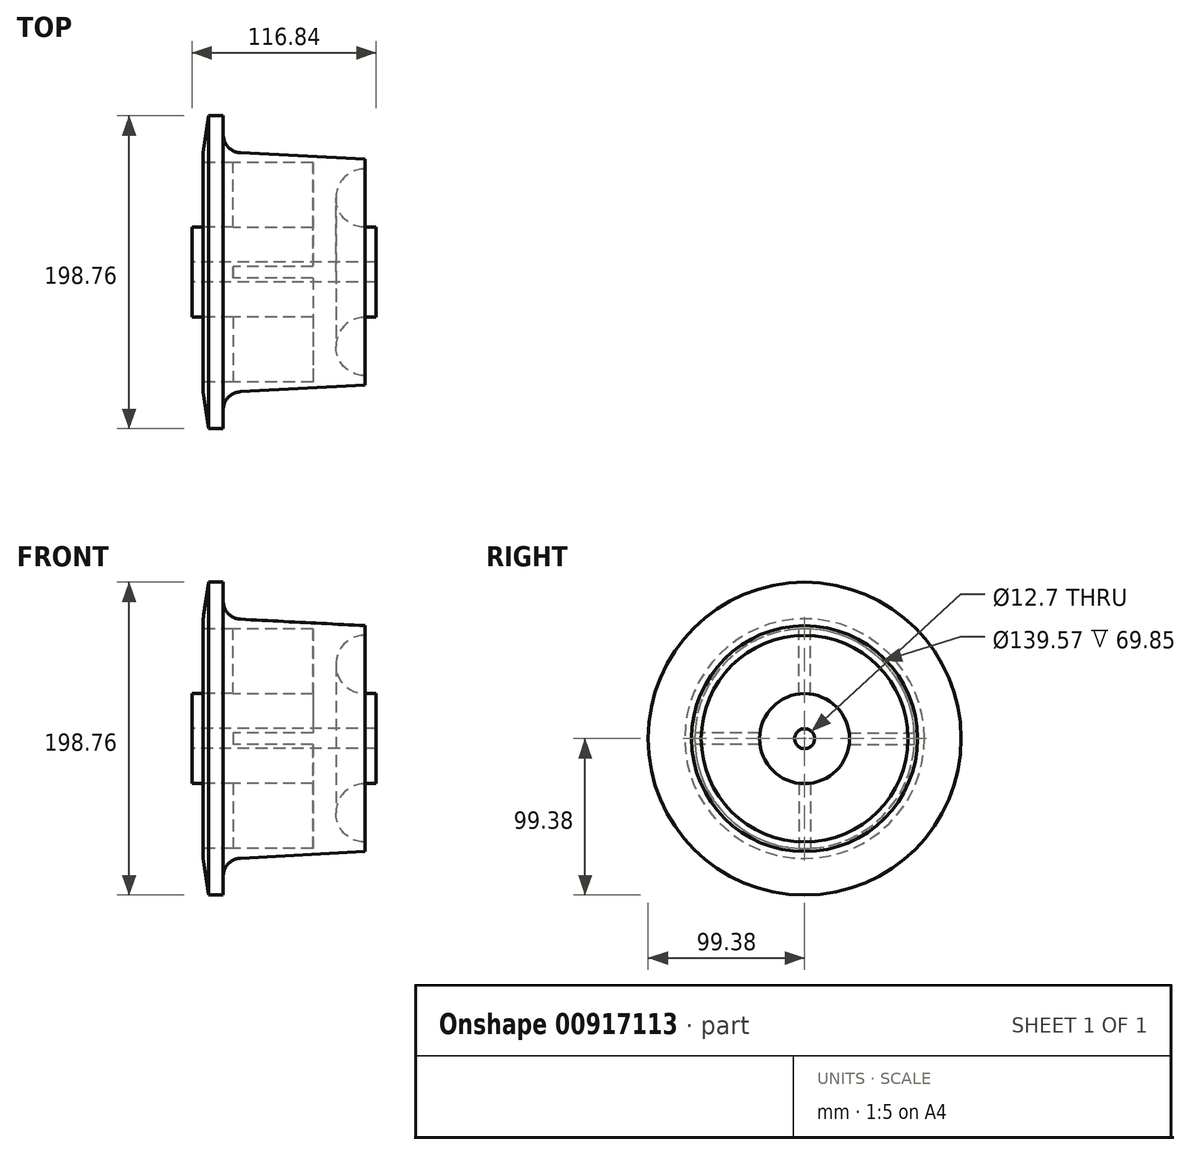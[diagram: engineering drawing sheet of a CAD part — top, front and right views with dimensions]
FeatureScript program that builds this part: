
annotation { "Feature Type Name" : "Feature", "Feature Type Description" : "" }
export const myFeature = defineFeature(function(context is Context, id is Id, definition is map)
    precondition{}
    {
        {
            var Q0;
            Q0=qCreatedBy(makeId("Front.planeOp"),FACE);
            var sketch = newSketch(context, id + "F0", { "sketchPlane" : qUnion([Q0])});
            skLineSegment(sketch, "E0", {"start": v(0, 6.35) * mm, "end": v(0, 0) * mm, "construction": true});
            skLineSegment(sketch, "E1", {"start": v(0, 6.35) * mm, "end": v(116.84, 6.35) * mm});
            skLineSegment(sketch, "E2", {"start": v(116.84, 6.35) * mm, "end": v(116.84, 28.58) * mm});
            skLineSegment(sketch, "E3", {"start": v(116.84, 28.58) * mm, "end": v(0, 28.58) * mm});
            skLineSegment(sketch, "E4", {"start": v(0, 28.58) * mm, "end": v(0, 6.35) * mm});
            skLineSegment(sketch, "E5", {"start": v(109.85, 28.58) * mm, "end": v(109.85, 71.76) * mm});
            skLineSegment(sketch, "E6", {"start": v(0, 99.38) * mm, "end": v(-18.57, 99.38) * mm, "construction": true});
            skLineSegment(sketch, "E7", {"start": v(6.99, 28.58) * mm, "end": v(6.99, 68.9) * mm});
            skLineSegment(sketch, "E8", {"start": v(6.99, 68.9) * mm, "end": v(21.01, 68.9) * mm, "construction": true});
            skLineSegment(sketch, "E9", {"start": v(6.99, 68.9) * mm, "end": v(6.99, 76.14) * mm});
            skLineSegment(sketch, "E10", {"start": v(6.99, 99.38) * mm, "end": v(10.54, 99.38) * mm, "construction": true});
            skLineSegment(sketch, "E11", {"start": v(6.99, 76.14) * mm, "end": v(10.54, 99.38) * mm});
            skLineSegment(sketch, "E12", {"start": v(10.54, 99.38) * mm, "end": v(19.81, 99.38) * mm});
            skLineSegment(sketch, "E13", {"start": v(19.81, 99.38) * mm, "end": v(19.81, 87.31) * mm});
            skLineSegment(sketch, "E14", {"start": v(109.85, 71.76) * mm, "end": v(30.64, 75.9) * mm});
            skArc(sketch, "E15", {"start": v(19.81, 87.31) * mm, "mid": v(22.95, 79.45) * mm, "end": v(30.64, 75.9) * mm});
            skLineSegment(sketch, "E16", {"start": v(0, 0) * mm, "end": v(91.98, 0) * mm, "construction": true});
            skPoint(sketch, "E17", {"position": v(22.95, 79.45) * mm});
            skSolve(sketch);
        }
        {
            var Q0;
            Q0=makeQuery(id+"F0.imprint","IMPRINT",FACE,{"disambiguationData":[TD([[makeQuery(id+"F0.imprint","IMPRINT",EDGE,{"derivedFrom":sQuery(id+"F0.wireOp",EDGE,"E1")}),1.0]])]});
            var Q1;
            {var subQ1=sQuery(id+"F0.wireOp",EDGE,"E5");Q1=makeQuery(id+"F0.imprint","IMPRINT",FACE,{"disambiguationData":[TD([[makeQuery(id+"F0.imprint","IMPRINT",EDGE,{"derivedFrom":subQ1}),1.0]])]});}
            var Q2;
            Q2=sQuery(id+"F0.wireOp",EDGE,"E16");
            revolve(context, id + "F1", {"surfaceOperationType" : NewSurfaceOperationType.NEW, "entities" : qUnion([Q0, Q1]), "axis" : qUnion([Q2]), "revolveType" : RevolveType.FULL});
        }
        {
            var Q0;
            Q0=qCreatedBy(makeId("Front.planeOp"),FACE);
            var sketch = newSketch(context, id + "F2", { "sketchPlane" : qUnion([Q0])});
            skLineSegment(sketch, "E18.0", {"start": v(109.85, -71.76) * mm, "end": v(109.85, 71.76) * mm});
            skLineSegment(sketch, "E19", {"start": v(109.85, 0) * mm, "end": v(85.08, 0) * mm, "construction": true});
            skLineSegment(sketch, "E20", {"start": v(109.85, 65.66) * mm, "end": v(128.1, 65.66) * mm, "construction": true});
            skLineSegment(sketch, "E21", {"start": v(109.85, 47.12) * mm, "end": v(125.43, 47.12) * mm, "construction": true});
            skArc(sketch, "E22", {"start": v(109.85, 65.66) * mm, "mid": v(91.31, 47.12) * mm, "end": v(109.85, 28.58) * mm});
            skSolve(sketch);
        }
        {
            var Q0;
            {var subQ0=sQuery(id+"F2.wireOp",EDGE,"E22");Q0=makeQuery(id+"F2.imprint","IMPRINT",FACE,{"disambiguationData":[TD([[makeQuery(id+"F2.imprint","IMPRINT",EDGE,{"derivedFrom":subQ0}),1.0]])]});}
            var Q1;
            Q1=sQuery(id+"F2.wireOp",EDGE,"E19");
            revolve(context, id + "F3", {"operationType" : NewBodyOperationType.REMOVE, "surfaceOperationType" : NewSurfaceOperationType.NEW, "entities" : qUnion([Q0]), "axis" : qUnion([Q1]), "revolveType" : RevolveType.FULL, "oppositeDirection" : true});
        }
        {
            var Q0;
            Q0=makeQuery(id+"F1.opRevolve","SWEPT_FACE",FACE,{"disambiguationData":[OSD([sQuery(id+"F0.wireOp",EDGE,"E7"),sQuery(id+"F0.wireOp",EDGE,"E9")])]});
            var sketch = newSketch(context, id + "F4", { "sketchPlane" : qUnion([Q0])});
            skCircle(sketch, "E23.0", {"center": v(0, 0) * mm, "radius": 76.14 * mm});
            skCircle(sketch, "E24.0", {"center": v(0, 0) * mm, "radius": 28.58 * mm});
            skLineSegment(sketch, "E25", {"start": v(0, 28.58) * mm, "end": v(0, 76.14) * mm, "construction": true});
            skLineSegment(sketch, "E26", {"start": v(28.58, 0) * mm, "end": v(76.14, 0) * mm, "construction": true});
            skLineSegment(sketch, "E27.0", {"start": v(3.62, 28.34) * mm, "end": v(3.62, 76.05) * mm});
            skLineSegment(sketch, "E28.0", {"start": v(-3.62, 28.34) * mm, "end": v(-3.62, 76.05) * mm});
            skLineSegment(sketch, "E29", {"start": v(0, 0) * mm, "end": v(14.85, 0) * mm, "construction": true});
            skLineSegment(sketch, "E30", {"start": v(0, 0) * mm, "end": v(0, 14.37) * mm, "construction": true});
            skLineSegment(sketch, "E31.0", {"start": v(28.34, -3.62) * mm, "end": v(76.05, -3.62) * mm});
            skLineSegment(sketch, "E32.0", {"start": v(28.34, 3.62) * mm, "end": v(76.05, 3.62) * mm});
            skLineSegment(sketch, "E33.MirrorCS", {"start": v(3.62, -28.34) * mm, "end": v(3.62, -76.05) * mm});
            skLineSegment(sketch, "E34.MirrorCS", {"start": v(-3.62, -28.34) * mm, "end": v(-3.62, -76.05) * mm});
            skLineSegment(sketch, "E35.MirrorCS", {"start": v(-28.34, 3.62) * mm, "end": v(-76.05, 3.62) * mm});
            skLineSegment(sketch, "E36.MirrorCS", {"start": v(-28.34, -3.62) * mm, "end": v(-76.05, -3.62) * mm});
            skCircle(sketch, "E37.0", {"center": v(0, 0) * mm, "radius": 69.79 * mm});
            skSolve(sketch);
        }
        {
            var Q0;
            {var subQ0=sQuery(id+"F4.wireOp",EDGE,"E31.0");var subQ1=sQuery(id+"F4.wireOp",EDGE,"E24.0");var subQ2=makeQuery(id+"F4.imprint","INTERSECT",VERTEX,{"derivedFrom":[subQ1,subQ0]});Q0=makeQuery(id+"F4.imprint","IMPRINT",FACE,{"disambiguationData":[TD([[makeQuery(id+"F4.imprint","IMPRINT",EDGE,{"disambiguationData":[TD([[subQ2,1.0]])],"derivedFrom":subQ1}),-1.0]])]});}
            var Q1;
            {var subQ0=sQuery(id+"F4.wireOp",EDGE,"E34.MirrorCS");var subQ1=sQuery(id+"F4.wireOp",EDGE,"E24.0");var subQ2=makeQuery(id+"F4.imprint","INTERSECT",VERTEX,{"derivedFrom":[subQ1,subQ0]});Q1=makeQuery(id+"F4.imprint","IMPRINT",FACE,{"disambiguationData":[TD([[makeQuery(id+"F4.imprint","IMPRINT",EDGE,{"disambiguationData":[TD([[subQ2,1.0]])],"derivedFrom":subQ1}),-1.0]])]});}
            var Q2;
            {var subQ0=sQuery(id+"F4.wireOp",EDGE,"E28.0");var subQ1=sQuery(id+"F4.wireOp",EDGE,"E24.0");var subQ2=makeQuery(id+"F4.imprint","INTERSECT",VERTEX,{"derivedFrom":[subQ1,subQ0]});Q2=makeQuery(id+"F4.imprint","IMPRINT",FACE,{"disambiguationData":[TD([[makeQuery(id+"F4.imprint","IMPRINT",EDGE,{"disambiguationData":[TD([[subQ2,-1.0]])],"derivedFrom":subQ1}),-1.0]])]});}
            var Q3;
            {var subQ0=sQuery(id+"F4.wireOp",EDGE,"E27.0");var subQ1=sQuery(id+"F4.wireOp",EDGE,"E24.0");var subQ2=makeQuery(id+"F4.imprint","INTERSECT",VERTEX,{"derivedFrom":[subQ1,subQ0]});Q3=makeQuery(id+"F4.imprint","IMPRINT",FACE,{"disambiguationData":[TD([[makeQuery(id+"F4.imprint","IMPRINT",EDGE,{"disambiguationData":[TD([[subQ2,1.0]])],"derivedFrom":subQ1}),-1.0]])]});}
            extrude(context, id + "F5", {"entities" : qUnion([Q0, Q1, Q2, Q3]), "operationType" : NewBodyOperationType.REMOVE, "oppositeDirection" : true, "depth" : 69.85 * mm, "offsetDistance" : 25.4 * mm});
        }
        {
            var Q0;
            {var subQ0=sQuery(id+"F4.wireOp",EDGE,"E35.MirrorCS");var subQ1=sQuery(id+"F4.wireOp",EDGE,"E24.0");var subQ2=makeQuery(id+"F4.imprint","INTERSECT",VERTEX,{"derivedFrom":[subQ1,subQ0]});Q0=makeQuery(id+"F4.imprint","IMPRINT",FACE,{"disambiguationData":[TD([[makeQuery(id+"F4.imprint","IMPRINT",EDGE,{"disambiguationData":[TD([[subQ2,-1.0]])],"derivedFrom":subQ1}),-1.0]])]});}
            var Q1;
            {var subQ0=sQuery(id+"F4.wireOp",EDGE,"E27.0");var subQ1=sQuery(id+"F4.wireOp",EDGE,"E24.0");var subQ2=makeQuery(id+"F4.imprint","INTERSECT",VERTEX,{"derivedFrom":[subQ1,subQ0]});Q1=makeQuery(id+"F4.imprint","IMPRINT",FACE,{"disambiguationData":[TD([[makeQuery(id+"F4.imprint","IMPRINT",EDGE,{"disambiguationData":[TD([[subQ2,-1.0]])],"derivedFrom":subQ1}),-1.0]])]});}
            var Q2;
            {var subQ0=sQuery(id+"F4.wireOp",EDGE,"E31.0");var subQ1=sQuery(id+"F4.wireOp",EDGE,"E24.0");var subQ2=makeQuery(id+"F4.imprint","INTERSECT",VERTEX,{"derivedFrom":[subQ1,subQ0]});Q2=makeQuery(id+"F4.imprint","IMPRINT",FACE,{"disambiguationData":[TD([[makeQuery(id+"F4.imprint","IMPRINT",EDGE,{"disambiguationData":[TD([[subQ2,-1.0]])],"derivedFrom":subQ1}),-1.0]])]});}
            var Q3;
            {var subQ0=sQuery(id+"F4.wireOp",EDGE,"E33.MirrorCS");var subQ1=sQuery(id+"F4.wireOp",EDGE,"E24.0");var subQ2=makeQuery(id+"F4.imprint","INTERSECT",VERTEX,{"derivedFrom":[subQ1,subQ0]});Q3=makeQuery(id+"F4.imprint","IMPRINT",FACE,{"disambiguationData":[TD([[makeQuery(id+"F4.imprint","IMPRINT",EDGE,{"disambiguationData":[TD([[subQ2,1.0]])],"derivedFrom":subQ1}),-1.0]])]});}
            extrude(context, id + "F6", {"entities" : qUnion([Q0, Q1, Q2, Q3]), "operationType" : NewBodyOperationType.REMOVE, "oppositeDirection" : true, "depth" : 19.05 * mm, "offsetDistance" : 25.4 * mm});
        }
    });
